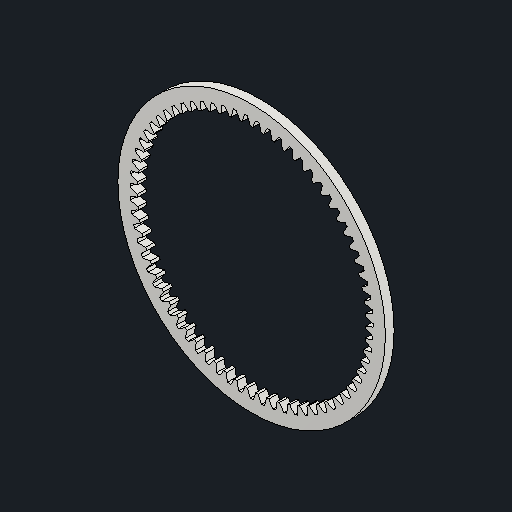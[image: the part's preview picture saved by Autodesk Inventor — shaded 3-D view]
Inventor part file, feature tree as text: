
AUTODESK INVENTOR PART (.ipt)
format: ipt  version: 2023.2 (Build 272271030, 271C)  size: 403,456 bytes
history: native  units: mm (DEFAULTED — no unit token found)
features: plane x3, other x3, sketch x2, extrude x1
ambient origin geometry x8: Origin, YZ Plane, XZ Plane, XY Plane, X Axis, Y Axis, Z Axis, Center Point
bodies: Solid1 (feature_tree)
feature tree (9):
  extrude  "Extrusion1"  Depth=5.0mm TaperAngle=0.0deg
  plane  "Work Plane2"
  plane  "Work Plane8"
  plane  "Work Plane9"
  other  "Spur Gear"
  sketch  "Sketch1"  dims[d0=152.9mm d1=5.0mm d2=0.0mm]
  sketch  "Sketch2"  dims[d3=134.0mm d4=10.0mm d5=0.0mm d16=51.0mm d17=0.0mm d34=0.468894mm d39=0.0mm d45=0.0mm d47=51.0mm d50=0.0mm d51=0.0mm d52=51.0mm]
  other  "Srf1"
  other  "Pitch Diameter"
